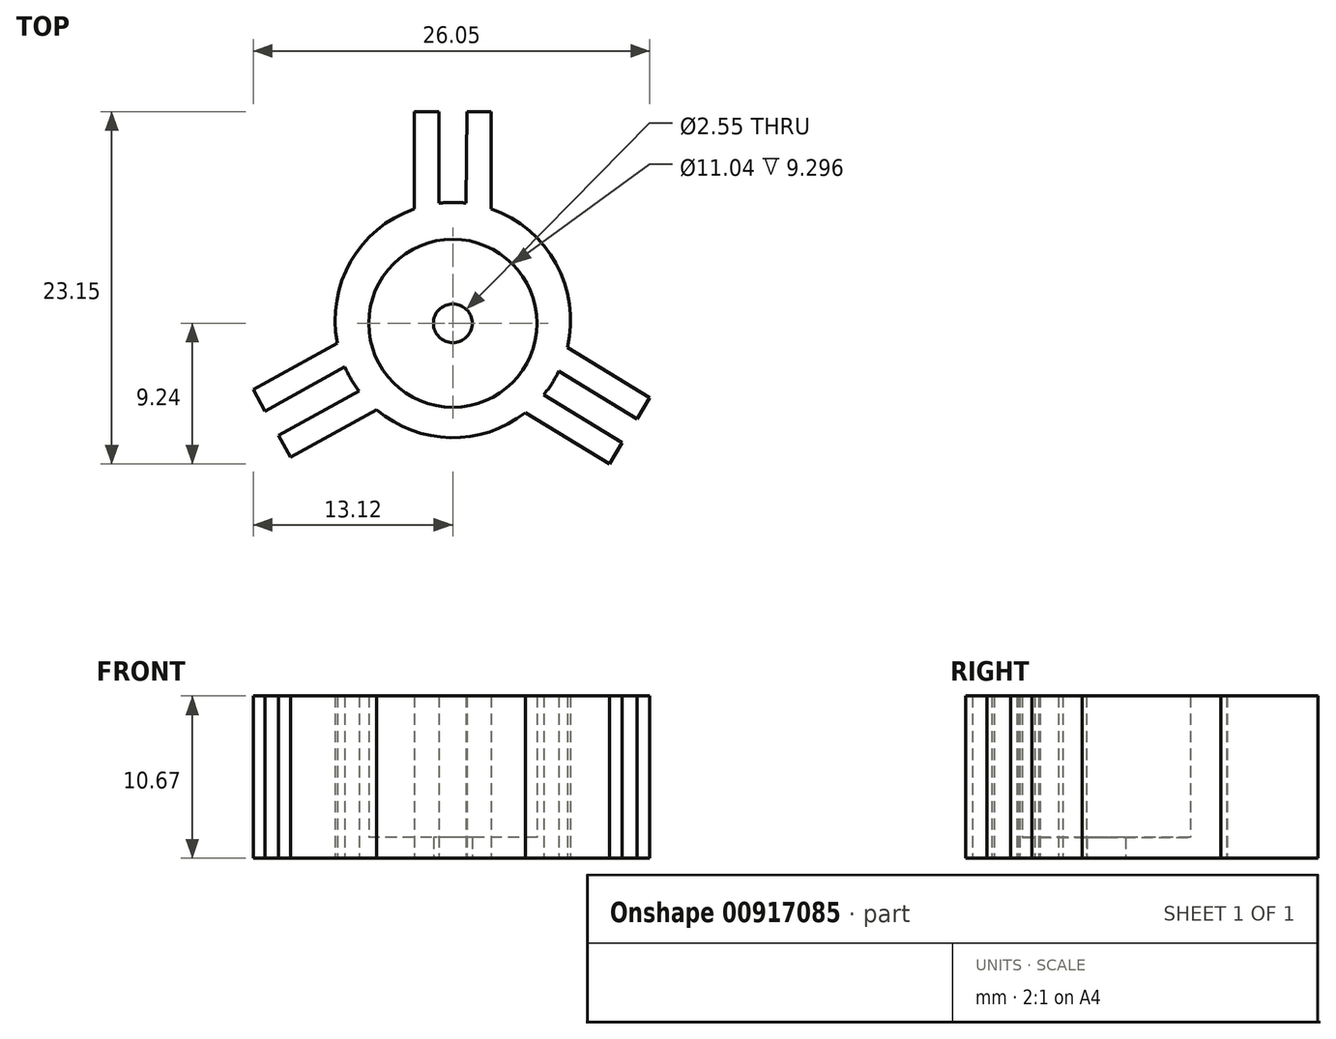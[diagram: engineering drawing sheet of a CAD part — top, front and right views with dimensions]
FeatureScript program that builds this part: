
annotation { "Feature Type Name" : "Feature", "Feature Type Description" : "" }
export const myFeature = defineFeature(function(context is Context, id is Id, definition is map)
    precondition{}
    {
        {
            var Q0;
            Q0=qCreatedBy(makeId("Top.planeOp"),FACE);
            var sketch = newSketch(context, id + "F0", { "sketchPlane" : qUnion([Q0])});
            skCircle(sketch, "E0", {"center": v(0, 0) * mm, "radius": 5.52 * mm});
            skCircle(sketch, "E1", {"center": v(0, 0.21) * mm, "radius": 7.73 * mm});
            skLineSegment(sketch, "E2.right", {"start": v(-0.93, 7.89) * mm, "end": v(-0.95, 7.9) * mm});
            skPoint(sketch, "E3.orphan", {"position": v(0, 13.9) * mm});
            skPoint(sketch, "E4.start.orphan", {"position": v(0.42, 13.9) * mm});
            skPoint(sketch, "E5.end.orphan", {"position": v(0.1, 13.9) * mm});
            skPoint(sketch, "E6.end.orphan", {"position": v(-0.1, 13.9) * mm});
            skPoint(sketch, "E7.end.orphan", {"position": v(-0.1, 0) * mm});
            skPoint(sketch, "E2.bottom.start.orphan", {"position": v(0.85, 0) * mm});
            skLineSegment(sketch, "E8.trimOffspring", {"start": v(-7, -3.88) * mm, "end": v(-7.04, -3.88) * mm});
            skPoint(sketch, "E9.end.orphan", {"position": v(-0.25, 7.94) * mm});
            skPoint(sketch, "E10.end.orphan", {"position": v(0.25, 7.94) * mm});
            skPoint(sketch, "E11.orphan", {"position": v(0.85, 13.9) * mm});
            skPoint(sketch, "E12.trimOffspring.end.orphan", {"position": v(-11.05, 13.9) * mm});
            skLineSegment(sketch, "E13.top", {"start": v(-0.91, 13.9) * mm, "end": v(-2.54, 13.9) * mm});
            skLineSegment(sketch, "E13.left", {"start": v(0, 7.94) * mm, "end": v(0, 7.95) * mm});
            skLineSegment(sketch, "E13.right", {"start": v(-2.54, 7.52) * mm, "end": v(-2.54, 13.9) * mm});
            skLineSegment(sketch, "E14", {"start": v(-12.33, -5.78) * mm, "end": v(-13.12, -4.36) * mm});
            skLineSegment(sketch, "E15", {"start": v(-13.12, -4.36) * mm, "end": v(-7.58, -1.3) * mm});
            skLineSegment(sketch, "E16", {"start": v(-5, -5.68) * mm, "end": v(-10.66, -8.8) * mm});
            skLineSegment(sketch, "E17", {"start": v(-11.45, -7.38) * mm, "end": v(-10.66, -8.8) * mm});
            skLineSegment(sketch, "E18.right", {"start": v(2.53, 7.52) * mm, "end": v(2.53, 13.9) * mm});
            skLineSegment(sketch, "E19", {"start": v(12.1, -6.28) * mm, "end": v(12.93, -4.9) * mm});
            skLineSegment(sketch, "E20", {"start": v(12.93, -4.9) * mm, "end": v(7.52, -1.6) * mm});
            skLineSegment(sketch, "E21", {"start": v(11.14, -7.85) * mm, "end": v(10.29, -9.24) * mm});
            skArc(sketch, "E22.trimOffspring", {"start": v(-0.91, 7.9) * mm, "mid": v(-0.93, 7.9) * mm, "end": v(-0.95, 7.9) * mm, "construction": true});
            skLineSegment(sketch, "E23", {"start": v(-12.33, -5.78) * mm, "end": v(-7.09, -2.88) * mm});
            skLineSegment(sketch, "E24", {"start": v(-7.09, -2.88) * mm, "end": v(-12.33, -5.78) * mm});
            skLineSegment(sketch, "E25", {"start": v(-11.45, -7.38) * mm, "end": v(-6.16, -4.46) * mm});
            skLineSegment(sketch, "E26", {"start": v(-0.91, 13.9) * mm, "end": v(-0.91, 7.9) * mm});
            skLineSegment(sketch, "E27", {"start": v(0.91, 13.9) * mm, "end": v(0.86, 7.9) * mm});
            skPoint(sketch, "E28.orphan", {"position": v(0.85, 6.25) * mm});
            skLineSegment(sketch, "E29", {"start": v(12.1, -6.28) * mm, "end": v(6.96, -3.15) * mm});
            skLineSegment(sketch, "E30", {"start": v(6.96, -3.15) * mm, "end": v(12.1, -6.28) * mm});
            skLineSegment(sketch, "E31", {"start": v(11.14, -7.85) * mm, "end": v(5.97, -4.7) * mm});
            skLineSegment(sketch, "E32.trimOffspring", {"start": v(0.91, 13.9) * mm, "end": v(2.53, 13.9) * mm});
            skLineSegment(sketch, "E33.trimOffspring", {"start": v(4.77, -5.88) * mm, "end": v(10.29, -9.24) * mm});
            skCircle(sketch, "E34", {"center": v(0, 0) * mm, "radius": 1.27 * mm});
            skSolve(sketch);
        }
        {
            var Q0;
            Q0=makeQuery(id+"F0.imprint","IMPRINT",FACE,{"disambiguationData":[TD([[makeQuery(id+"F0.imprint","IMPRINT",EDGE,{"derivedFrom":sQuery(id+"F0.wireOp",EDGE,"E0")}),1.0]])]});
            extrude(context, id + "F1", {"entities" : qUnion([Q0]), "depth" : 1.37 * mm, "offsetDistance" : 25.4 * mm});
        }
        {
            var Q0;
            Q0=makeQuery(id+"F0.imprint","IMPRINT",FACE,{"disambiguationData":[TD([[makeQuery(id+"F0.imprint","IMPRINT",EDGE,{"derivedFrom":sQuery(id+"F0.wireOp",EDGE,"E0")}),-1.0]])]});
            extrude(context, id + "F2", {"entities" : qUnion([Q0]), "operationType" : NewBodyOperationType.ADD, "depth" : 7.7 * mm, "offsetDistance" : 25.4 * mm});
        }
        {
            var Q0;
            Q0 = qSketchRegion(id + "F0", true);
            extrude(context, id + "F3", {"entities" : qUnion([Q0]), "operationType" : NewBodyOperationType.ADD, "depth" : 9.65 * mm, "offsetDistance" : 25.4 * mm});
        }
        {
            var Q0;
            Q0 = qSketchRegion(id + "F0", true);
            extrude(context, id + "F4", {"entities" : qUnion([Q0]), "operationType" : NewBodyOperationType.ADD, "depth" : 10.67 * mm, "offsetDistance" : 25.4 * mm});
        }
    });
